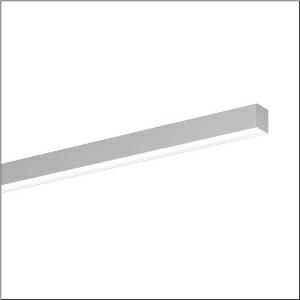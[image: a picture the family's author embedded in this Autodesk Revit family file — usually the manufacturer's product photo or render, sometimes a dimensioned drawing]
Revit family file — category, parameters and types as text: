
# Revit family: silica_r__21_51mx20db32sb_b045
name_source: partatom
category: Lighting Fixtures
units: mm (PartAtom-declared; Revit-internal decimal feet)

## family parameters
Cut with Voids When Loaded = No
Host = Face
Light Source = No
Part Type = Normal
Room Calculation Point = No
Round Connector Dimension = Use Diameter
Shared = No

## types (1)
- --- (1 x LED, 3000 lm, 20.2 W, 3000K)
    Apparent Load = 20 VA
    CIE Flux Codes = 48 79 96 100 100
    Color Rendering = 80
    Color Temperature = 3000K
    Default Elevation = 1800 mm
    Description = Silica® 21, office luminaire, primary optical cover: cover, of PMMA, opal, light emission: direct distribution, primary light characteristic: symmetric, installation type: surface-mounted, LED, rated luminous flux: 3.000lm, luminous efficacy: 149lm/W, light colour: 830, colour temperature: 3000K, control gear: DALI 2, with terminal, 3+2-pole, max. 2.5mm², mains connection: 220..240V, AC, 50/60Hz, luminaire housing, of aluminium, metallic grey (RAL 9006), length: 1.504mm, width: 53mm, height: 53mm, protection rating (complete): IP20, insulation class (complete): insulation class I (protective earthing), certification: CE, permissible operating ambient temperature: 0..+35°C, standard: EN 50419, packaging unit: 1 piece
    Height = 53 mm
    Lamp = 1 x LED
    Lamp Light Flux = 3000 lm
    Lamp Power = 20.2 W
    Lamp count = 1
    Length = 1504 mm
    Luminous efficacy = 149 lm/W
    Manufacturer = Siteco
    ModVariant = No
    Model = 51MX20DB32SB
    Mounting Place = Ceiling
    Mounting Type = Surface mounted
    Number of Poles = 1
    OnlyDefault = Yes
    Power Factor = 1
    Product Name = Silica® 21
    Product group = office luminaire | ceiling mounted
    ProductGroupID = 302
    Protection Class = Protection class I
    Protection Degree = IP 20
    RLX_Detail_Level = 1
    RLX_Emergency_Light_Flux = 0 lm
    RLX_Emergency_Type = 0
    RLX_Emergency_Type_DB = No
    RlxData = <blob elided: 26089 chars, md5=d3e6557b>
    Socket = socket
    Standby Power = 0 W
    System Light Flux = 3000 lm
    System Power = 20 W
    Type Comments = factory setting: luminous flux: 100 % | dim-lin: 254 | 233 mA
    Type Image = l_1335933.jpg
    URL = http://relux.com
    VarID = @adj_117970
    Voltage = 0 V
    Weight = 0.00 kg
    Width = 53 mm

## geometry (parser evidence)
native form markers: Blend x4, Sweep x9
no freeform markers — native parametric forms only
